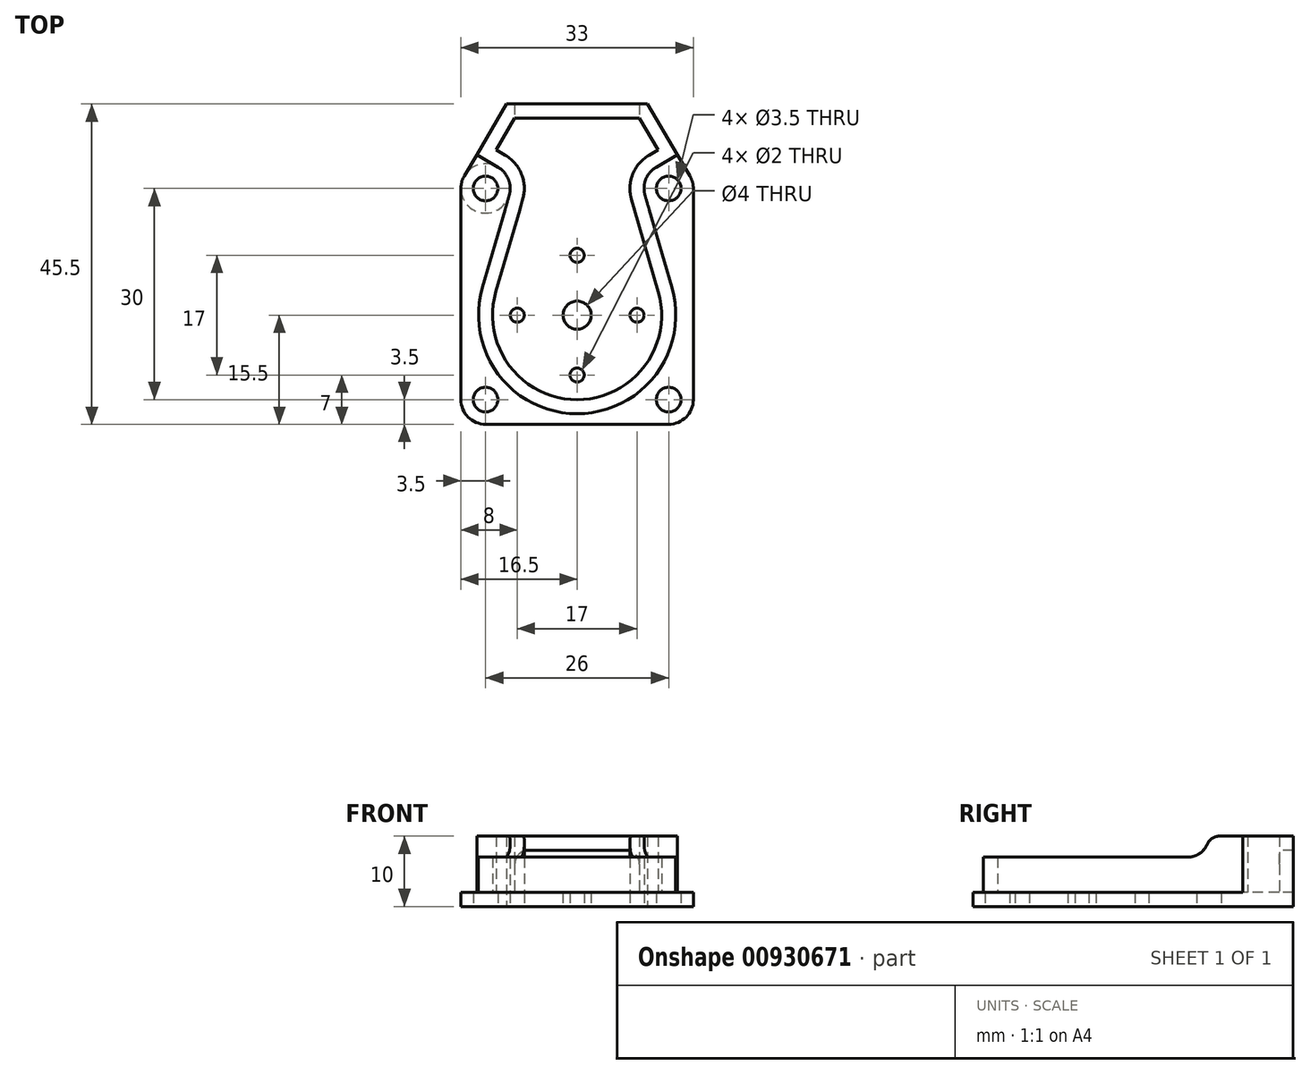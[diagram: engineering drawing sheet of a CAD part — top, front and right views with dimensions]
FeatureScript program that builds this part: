
annotation { "Feature Type Name" : "Feature", "Feature Type Description" : "" }
export const myFeature = defineFeature(function(context is Context, id is Id, definition is map)
    precondition{}
    {
        {
            var Q0;
            Q0=qCreatedBy(makeId("Top.planeOp"),FACE);
            var sketch = newSketch(context, id + "F0", { "sketchPlane" : qUnion([Q0])});
            skCircle(sketch, "E0", {"center": v(0, 0) * mm, "radius": 1.75 * mm});
            skCircle(sketch, "E1", {"center": v(0, 30) * mm, "radius": 1.75 * mm});
            skCircle(sketch, "E2", {"center": v(26, 30) * mm, "radius": 1.75 * mm});
            skCircle(sketch, "E3", {"center": v(26, 0) * mm, "radius": 1.75 * mm});
            skLineSegment(sketch, "E4.left", {"start": v(0, 30) * mm, "end": v(0, 0) * mm, "construction": true});
            skCircle(sketch, "E5", {"center": v(13, 12) * mm, "radius": 9.85 * mm, "construction": true});
            skLineSegment(sketch, "E6", {"start": v(13, 21.85) * mm, "end": v(13, 2.15) * mm, "construction": true});
            skLineSegment(sketch, "E7", {"start": v(3.15, 12) * mm, "end": v(22.85, 12) * mm, "construction": true});
            skCircle(sketch, "E8", {"center": v(13, 12) * mm, "radius": 2 * mm});
            skCircle(sketch, "E9", {"center": v(4.5, 12) * mm, "radius": 1 * mm});
            skCircle(sketch, "E10", {"center": v(21.5, 12) * mm, "radius": 1 * mm});
            skCircle(sketch, "E11", {"center": v(13, 20.5) * mm, "radius": 1 * mm});
            skCircle(sketch, "E12", {"center": v(13, 3.5) * mm, "radius": 1 * mm});
            skLineSegment(sketch, "E13", {"start": v(3, 42) * mm, "end": v(23, 42) * mm});
            skLineSegment(sketch, "E14", {"start": v(0, 30) * mm, "end": v(26, 30) * mm, "construction": true});
            skLineSegment(sketch, "E15", {"start": v(0, 0) * mm, "end": v(26, 0) * mm, "construction": true});
            skLineSegment(sketch, "E16.trimOffspring", {"start": v(-3.02, 31.77) * mm, "end": v(3, 42) * mm});
            skLineSegment(sketch, "E17.trimOffspring", {"start": v(29.02, 31.77) * mm, "end": v(23, 42) * mm});
            skLineSegment(sketch, "E18", {"start": v(26, 30) * mm, "end": v(26, 0) * mm, "construction": true});
            skLineSegment(sketch, "E19", {"start": v(-3.5, 30) * mm, "end": v(-3.5, 0) * mm});
            skLineSegment(sketch, "E20", {"start": v(0, -3.5) * mm, "end": v(26, -3.5) * mm});
            skLineSegment(sketch, "E21", {"start": v(29.5, 30) * mm, "end": v(29.5, 0) * mm});
            skArc(sketch, "E22", {"start": v(-3.5, 0) * mm, "mid": v(-2.47, -2.47) * mm, "end": v(0, -3.5) * mm});
            skArc(sketch, "E23", {"start": v(26, -3.5) * mm, "mid": v(28.47, -2.47) * mm, "end": v(29.5, 0) * mm});
            skArc(sketch, "E24", {"start": v(-3.02, 31.77) * mm, "mid": v(-3.38, 30.92) * mm, "end": v(-3.5, 30) * mm});
            skArc(sketch, "E25", {"start": v(29.5, 30) * mm, "mid": v(29.38, 30.92) * mm, "end": v(29.02, 31.77) * mm});
            skSolve(sketch);
        }
        {
            var Q0;
            Q0=qSketchRegion(id+"F0",true);
            extrude(context, id + "F1", {"entities" : qUnion([Q0]), "depth" : 2 * mm, "offsetDistance" : 25 * mm});
        }
        {
            var Q0;
            Q0=makeQuery(id+"F1.opExtrude","CAP_FACE",FACE,{"disambiguationData":[OSD([sQuery(id+"F0.wireOp",EDGE,"E0"),sQuery(id+"F0.wireOp",EDGE,"E1"),sQuery(id+"F0.wireOp",EDGE,"E2"),sQuery(id+"F0.wireOp",EDGE,"E3"),sQuery(id+"F0.wireOp",EDGE,"E8"),sQuery(id+"F0.wireOp",EDGE,"E9"),sQuery(id+"F0.wireOp",EDGE,"E10"),sQuery(id+"F0.wireOp",EDGE,"E11"),sQuery(id+"F0.wireOp",EDGE,"E12"),sQuery(id+"F0.wireOp",EDGE,"E13"),sQuery(id+"F0.wireOp",EDGE,"E16.trimOffspring"),sQuery(id+"F0.wireOp",EDGE,"E17.trimOffspring"),sQuery(id+"F0.wireOp",EDGE,"E19"),sQuery(id+"F0.wireOp",EDGE,"E20"),sQuery(id+"F0.wireOp",EDGE,"E21"),sQuery(id+"F0.wireOp",EDGE,"E22"),sQuery(id+"F0.wireOp",EDGE,"E23"),sQuery(id+"F0.wireOp",EDGE,"E24"),sQuery(id+"F0.wireOp",EDGE,"E25")])],"isStart":false});
            var sketch = newSketch(context, id + "F2", { "sketchPlane" : qUnion([Q0])});
            skLineSegment(sketch, "E26", {"start": v(0, 30) * mm, "end": v(26, 30) * mm, "construction": true});
            skLineSegment(sketch, "E27", {"start": v(3, 42) * mm, "end": v(23, 42) * mm});
            skLineSegment(sketch, "E28", {"start": v(23, 42) * mm, "end": v(27.24, 34.8) * mm});
            skLineSegment(sketch, "E29", {"start": v(27.24, 34.8) * mm, "end": v(24.23, 33.02) * mm});
            skArc(sketch, "E30", {"start": v(24.23, 33.02) * mm, "mid": v(22.75, 31.3) * mm, "end": v(22.64, 29.02) * mm});
            skArc(sketch, "E31", {"start": v(3.36, 29.02) * mm, "mid": v(3.25, 31.3) * mm, "end": v(1.77, 33.02) * mm});
            skLineSegment(sketch, "E32", {"start": v(3, 42) * mm, "end": v(-1.24, 34.8) * mm});
            skLineSegment(sketch, "E33", {"start": v(-1.24, 34.8) * mm, "end": v(1.77, 33.02) * mm});
            skLineSegment(sketch, "E34", {"start": v(4.14, 40) * mm, "end": v(1.5, 35.5) * mm});
            skLineSegment(sketch, "E35", {"start": v(1.5, 35.5) * mm, "end": v(2.79, 34.74) * mm});
            skLineSegment(sketch, "E36", {"start": v(4.14, 40) * mm, "end": v(21.86, 40) * mm});
            skLineSegment(sketch, "E37", {"start": v(21.86, 40) * mm, "end": v(24.5, 35.5) * mm});
            skLineSegment(sketch, "E38", {"start": v(24.5, 35.5) * mm, "end": v(23.21, 34.74) * mm});
            skArc(sketch, "E39", {"start": v(5.28, 28.47) * mm, "mid": v(5.11, 32.03) * mm, "end": v(2.79, 34.74) * mm});
            skArc(sketch, "E40", {"start": v(23.21, 34.74) * mm, "mid": v(20.89, 32.03) * mm, "end": v(20.72, 28.47) * mm});
            skArc(sketch, "E41", {"start": v(1.48, 15.34) * mm, "mid": v(13, 0) * mm, "end": v(24.52, 15.34) * mm});
            skArc(sketch, "E42", {"start": v(-0.45, 15.9) * mm, "mid": v(13, -2) * mm, "end": v(26.45, 15.9) * mm});
            skLineSegment(sketch, "E43", {"start": v(-0.45, 15.9) * mm, "end": v(3.36, 29.02) * mm});
            skLineSegment(sketch, "E44", {"start": v(22.64, 29.02) * mm, "end": v(26.45, 15.9) * mm});
            skLineSegment(sketch, "E45", {"start": v(20.72, 28.47) * mm, "end": v(24.52, 15.34) * mm});
            skLineSegment(sketch, "E46", {"start": v(5.28, 28.47) * mm, "end": v(1.48, 15.34) * mm});
            skSolve(sketch);
        }
        {
            var Q0;
            Q0=qSketchRegion(id+"F2",true);
            extrude(context, id + "F3", {"entities" : qUnion([Q0]), "operationType" : NewBodyOperationType.ADD, "depth" : 8 * mm, "offsetDistance" : 25 * mm});
        }
        {
            var Q0;
            Q0=makeQuery(id+"F3.opExtrude","SWEPT_FACE",FACE,{"disambiguationData":[OSD([sQuery(id+"F2.wireOp",EDGE,"E36")])]});
            var sketch = newSketch(context, id + "F4", { "sketchPlane" : qUnion([Q0])});
            skLineSegment(sketch, "E47.bottom", {"start": v(4.14, 2) * mm, "end": v(21.86, 2) * mm});
            skLineSegment(sketch, "E47.top", {"start": v(4.14, 8) * mm, "end": v(21.86, 8) * mm});
            skLineSegment(sketch, "E47.left", {"start": v(4.14, 2) * mm, "end": v(4.14, 8) * mm});
            skLineSegment(sketch, "E47.right", {"start": v(21.86, 2) * mm, "end": v(21.86, 8) * mm});
            skSolve(sketch);
        }
        {
            var Q0;
            Q0=qSketchRegion(id+"F4",true);
            extrude(context, id + "F5", {"entities" : qUnion([Q0]), "operationType" : NewBodyOperationType.REMOVE, "endBound" : BoundingType.UP_TO_NEXT, "oppositeDirection" : true, "depth" : 25 * mm, "offsetDistance" : 25 * mm});
        }
        {
            var Q0;
            Q0=makeQuery(id+"F5.boolean.opBoolean","COPY",EDGE,{"derivedFrom":makeQuery(id+"F5.opExtrude","SWEPT_EDGE",EDGE,{"disambiguationData":[OSD([sQuery(id+"F2.wireOp",EDGE,"E34"),sQuery(id+"F2.wireOp",EDGE,"E36"),sQuery(id+"F4.wireOp",EDGE,"E47.top"),sQuery(id+"F4.wireOp",EDGE,"E47.left")])]})});
            var Q1;
            Q1=makeQuery(id+"FvPu7uBZYHSXlxQ_1.boolean.opBoolean","COPY",EDGE,{"derivedFrom":makeQuery(id+"FvPu7uBZYHSXlxQ_1.opExtrude","SWEPT_EDGE",EDGE,{"disambiguationData":[OSD([sQuery(id+"F2.wireOp",EDGE,"87owH7vI-DY4W-UaA8-oZaw-rFrzevB4dvaM"),sQuery(id+"F2.wireOp",EDGE,"E39"),sQuery(id+"FQrBlxE3tJIOwN5_1.wireOp",EDGE,"wGyyUJUZ-AgT6-l7fz-nEv1-yPwmvjUjWFtQ.top"),sQuery(id+"FQrBlxE3tJIOwN5_1.wireOp",EDGE,"wGyyUJUZ-AgT6-l7fz-nEv1-yPwmvjUjWFtQ.right")])]})});
            var Q2;
            Q2=makeQuery(id+"FvPu7uBZYHSXlxQ_1.boolean.opBoolean","COPY",EDGE,{"derivedFrom":makeQuery(id+"FvPu7uBZYHSXlxQ_1.opExtrude","SWEPT_EDGE",EDGE,{"disambiguationData":[OSD([sQuery(id+"F2.wireOp",EDGE,"87owH7vI-DY4W-UaA8-oZaw-rFrzevB4dvaM"),sQuery(id+"F2.wireOp",EDGE,"E40"),sQuery(id+"FQrBlxE3tJIOwN5_1.wireOp",EDGE,"wGyyUJUZ-AgT6-l7fz-nEv1-yPwmvjUjWFtQ.top"),sQuery(id+"FQrBlxE3tJIOwN5_1.wireOp",EDGE,"wGyyUJUZ-AgT6-l7fz-nEv1-yPwmvjUjWFtQ.left")])]})});
            var Q3;
            Q3=makeQuery(id+"F5.boolean.opBoolean","COPY",EDGE,{"derivedFrom":makeQuery(id+"F5.opExtrude","SWEPT_EDGE",EDGE,{"disambiguationData":[OSD([sQuery(id+"F2.wireOp",EDGE,"E36"),sQuery(id+"F2.wireOp",EDGE,"E37"),sQuery(id+"F4.wireOp",EDGE,"E47.top"),sQuery(id+"F4.wireOp",EDGE,"E47.right")])]})});
            fillet(context, id + "F6", {"entities" : qUnion([Q0, Q1, Q2, Q3]), "radius" : 2 * mm, "tangentPropagation" : true, "allowEdgeOverflow" : false});
        }
        {
            var Q0;
            Q0=makeQuery(id+"F3.opExtrude","CAP_FACE",FACE,{"disambiguationData":[OSD([sQuery(id+"F2.wireOp",EDGE,"87owH7vI-DY4W-UaA8-oZaw-rFrzevB4dvaM"),sQuery(id+"F2.wireOp",EDGE,"E27"),sQuery(id+"F2.wireOp",EDGE,"E28"),sQuery(id+"F2.wireOp",EDGE,"E29"),sQuery(id+"F2.wireOp",EDGE,"E30"),sQuery(id+"F2.wireOp",EDGE,"E31"),sQuery(id+"F2.wireOp",EDGE,"E32"),sQuery(id+"F2.wireOp",EDGE,"E33"),sQuery(id+"F2.wireOp",EDGE,"E34"),sQuery(id+"F2.wireOp",EDGE,"E35"),sQuery(id+"F2.wireOp",EDGE,"E36"),sQuery(id+"F2.wireOp",EDGE,"E37"),sQuery(id+"F2.wireOp",EDGE,"E38"),sQuery(id+"F2.wireOp",EDGE,"E39"),sQuery(id+"F2.wireOp",EDGE,"E40"),sQuery(id+"F2.wireOp",EDGE,"E41"),sQuery(id+"F2.wireOp",EDGE,"E42"),sQuery(id+"F2.wireOp",EDGE,"E43"),sQuery(id+"F2.wireOp",EDGE,"E44"),sQuery(id+"F2.wireOp",EDGE,"n5o2zeqW-Y6Ct-pq06-zOnF-6KBVIWVYcsxy"),sQuery(id+"F2.wireOp",EDGE,"E45"),sQuery(id+"F2.wireOp",EDGE,"E46")])],"isStart":false});
            var sketch = newSketch(context, id + "F7", { "sketchPlane" : qUnion([Q0])});
            skLineSegment(sketch, "E48", {"start": v(5.28, 28.47) * mm, "end": v(1.48, 15.34) * mm});
            skLineSegment(sketch, "E49", {"start": v(3.36, 29.02) * mm, "end": v(-0.45, 15.9) * mm});
            skLineSegment(sketch, "E50", {"start": v(20.72, 28.47) * mm, "end": v(24.52, 15.34) * mm});
            skLineSegment(sketch, "E51", {"start": v(22.64, 29.02) * mm, "end": v(26.45, 15.9) * mm});
            skArc(sketch, "E52", {"start": v(1.48, 15.34) * mm, "mid": v(13, 0) * mm, "end": v(24.52, 15.34) * mm});
            skArc(sketch, "E53", {"start": v(-0.45, 15.9) * mm, "mid": v(13, -2) * mm, "end": v(26.45, 15.9) * mm});
            skLineSegment(sketch, "E54", {"start": v(3.5, 30) * mm, "end": v(5.5, 30) * mm});
            skLineSegment(sketch, "E55", {"start": v(20.5, 30) * mm, "end": v(22.5, 30) * mm});
            skArc(sketch, "E56", {"start": v(5.28, 28.47) * mm, "mid": v(5.45, 29.23) * mm, "end": v(5.5, 30) * mm});
            skArc(sketch, "E57", {"start": v(3.36, 29.02) * mm, "mid": v(3.47, 29.5) * mm, "end": v(3.5, 30) * mm});
            skArc(sketch, "E58", {"start": v(20.5, 30) * mm, "mid": v(20.55, 29.23) * mm, "end": v(20.72, 28.47) * mm});
            skArc(sketch, "E59", {"start": v(22.5, 30) * mm, "mid": v(22.53, 29.5) * mm, "end": v(22.64, 29.02) * mm});
            skSolve(sketch);
        }
        {
            var Q0;
            Q0=qSketchRegion(id+"F7",true);
            extrude(context, id + "F8", {"entities" : qUnion([Q0]), "operationType" : NewBodyOperationType.REMOVE, "oppositeDirection" : true, "depth" : 3 * mm, "offsetDistance" : 25 * mm});
        }
        {
            var Q0;
            Q0=makeQuery(id+"F8.boolean.opBoolean","COPY",EDGE,{"derivedFrom":makeQuery(id+"F8.opExtrude","CAP_EDGE",EDGE,{"disambiguationData":[OSD([sQuery(id+"F7.wireOp",EDGE,"E54")])],"isStart":false})});
            var Q1;
            Q1=makeQuery(id+"F8.boolean.opBoolean","COPY",EDGE,{"derivedFrom":makeQuery(id+"F8.opExtrude","CAP_EDGE",EDGE,{"disambiguationData":[OSD([sQuery(id+"F7.wireOp",EDGE,"E55")])],"isStart":false})});
            fillet(context, id + "F9", {"entities" : qUnion([Q0, Q1]), "radius" : 3 * mm, "tangentPropagation" : true, "allowEdgeOverflow" : false});
        }
        {
            var Q0;
            Q0=makeQuery(id+"F9.opFillet","BLEND_EDGE",EDGE,{"blendedFrom":[makeQuery(id+"F8.boolean.opBoolean","COPY",EDGE,{"derivedFrom":makeQuery(id+"F8.opExtrude","CAP_EDGE",EDGE,{"disambiguationData":[OSD([sQuery(id+"F7.wireOp",EDGE,"E54")])],"isStart":false})}),makeQuery(id+"F3.opExtrude","CAP_FACE",FACE,{"disambiguationData":[OSD([sQuery(id+"F2.wireOp",EDGE,"E27"),sQuery(id+"F2.wireOp",EDGE,"E28"),sQuery(id+"F2.wireOp",EDGE,"E29"),sQuery(id+"F2.wireOp",EDGE,"E30"),sQuery(id+"F2.wireOp",EDGE,"E31"),sQuery(id+"F2.wireOp",EDGE,"E32"),sQuery(id+"F2.wireOp",EDGE,"E33"),sQuery(id+"F2.wireOp",EDGE,"E34"),sQuery(id+"F2.wireOp",EDGE,"E35"),sQuery(id+"F2.wireOp",EDGE,"E36"),sQuery(id+"F2.wireOp",EDGE,"E37"),sQuery(id+"F2.wireOp",EDGE,"E38"),sQuery(id+"F2.wireOp",EDGE,"E39"),sQuery(id+"F2.wireOp",EDGE,"E40"),sQuery(id+"F2.wireOp",EDGE,"E41"),sQuery(id+"F2.wireOp",EDGE,"E42"),sQuery(id+"F2.wireOp",EDGE,"E43"),sQuery(id+"F2.wireOp",EDGE,"E44"),sQuery(id+"F2.wireOp",EDGE,"E45"),sQuery(id+"F2.wireOp",EDGE,"E46")])],"isStart":false})],"blendedInto":[makeQuery(id+"F3.opExtrude","CAP_FACE",FACE,{"disambiguationData":[OSD([sQuery(id+"F2.wireOp",EDGE,"E27"),sQuery(id+"F2.wireOp",EDGE,"E28"),sQuery(id+"F2.wireOp",EDGE,"E29"),sQuery(id+"F2.wireOp",EDGE,"E30"),sQuery(id+"F2.wireOp",EDGE,"E31"),sQuery(id+"F2.wireOp",EDGE,"E32"),sQuery(id+"F2.wireOp",EDGE,"E33"),sQuery(id+"F2.wireOp",EDGE,"E34"),sQuery(id+"F2.wireOp",EDGE,"E35"),sQuery(id+"F2.wireOp",EDGE,"E36"),sQuery(id+"F2.wireOp",EDGE,"E37"),sQuery(id+"F2.wireOp",EDGE,"E38"),sQuery(id+"F2.wireOp",EDGE,"E39"),sQuery(id+"F2.wireOp",EDGE,"E40"),sQuery(id+"F2.wireOp",EDGE,"E41"),sQuery(id+"F2.wireOp",EDGE,"E42"),sQuery(id+"F2.wireOp",EDGE,"E43"),sQuery(id+"F2.wireOp",EDGE,"E44"),sQuery(id+"F2.wireOp",EDGE,"E45"),sQuery(id+"F2.wireOp",EDGE,"E46")])],"isStart":false})]});
            var Q1;
            Q1=makeQuery(id+"F9.opFillet","BLEND_EDGE",EDGE,{"blendedFrom":[makeQuery(id+"F8.boolean.opBoolean","COPY",EDGE,{"derivedFrom":makeQuery(id+"F8.opExtrude","CAP_EDGE",EDGE,{"disambiguationData":[OSD([sQuery(id+"F7.wireOp",EDGE,"E55")])],"isStart":false})}),makeQuery(id+"F3.opExtrude","CAP_FACE",FACE,{"disambiguationData":[OSD([sQuery(id+"F2.wireOp",EDGE,"E27"),sQuery(id+"F2.wireOp",EDGE,"E28"),sQuery(id+"F2.wireOp",EDGE,"E29"),sQuery(id+"F2.wireOp",EDGE,"E30"),sQuery(id+"F2.wireOp",EDGE,"E31"),sQuery(id+"F2.wireOp",EDGE,"E32"),sQuery(id+"F2.wireOp",EDGE,"E33"),sQuery(id+"F2.wireOp",EDGE,"E34"),sQuery(id+"F2.wireOp",EDGE,"E35"),sQuery(id+"F2.wireOp",EDGE,"E36"),sQuery(id+"F2.wireOp",EDGE,"E37"),sQuery(id+"F2.wireOp",EDGE,"E38"),sQuery(id+"F2.wireOp",EDGE,"E39"),sQuery(id+"F2.wireOp",EDGE,"E40"),sQuery(id+"F2.wireOp",EDGE,"E41"),sQuery(id+"F2.wireOp",EDGE,"E42"),sQuery(id+"F2.wireOp",EDGE,"E43"),sQuery(id+"F2.wireOp",EDGE,"E44"),sQuery(id+"F2.wireOp",EDGE,"E45"),sQuery(id+"F2.wireOp",EDGE,"E46")])],"isStart":false})],"blendedInto":[makeQuery(id+"F3.opExtrude","CAP_FACE",FACE,{"disambiguationData":[OSD([sQuery(id+"F2.wireOp",EDGE,"E27"),sQuery(id+"F2.wireOp",EDGE,"E28"),sQuery(id+"F2.wireOp",EDGE,"E29"),sQuery(id+"F2.wireOp",EDGE,"E30"),sQuery(id+"F2.wireOp",EDGE,"E31"),sQuery(id+"F2.wireOp",EDGE,"E32"),sQuery(id+"F2.wireOp",EDGE,"E33"),sQuery(id+"F2.wireOp",EDGE,"E34"),sQuery(id+"F2.wireOp",EDGE,"E35"),sQuery(id+"F2.wireOp",EDGE,"E36"),sQuery(id+"F2.wireOp",EDGE,"E37"),sQuery(id+"F2.wireOp",EDGE,"E38"),sQuery(id+"F2.wireOp",EDGE,"E39"),sQuery(id+"F2.wireOp",EDGE,"E40"),sQuery(id+"F2.wireOp",EDGE,"E41"),sQuery(id+"F2.wireOp",EDGE,"E42"),sQuery(id+"F2.wireOp",EDGE,"E43"),sQuery(id+"F2.wireOp",EDGE,"E44"),sQuery(id+"F2.wireOp",EDGE,"E45"),sQuery(id+"F2.wireOp",EDGE,"E46")])],"isStart":false})]});
            fillet(context, id + "F10", {"entities" : qUnion([Q0, Q1]), "radius" : 2 * mm, "tangentPropagation" : true, "allowEdgeOverflow" : false});
        }
    });
